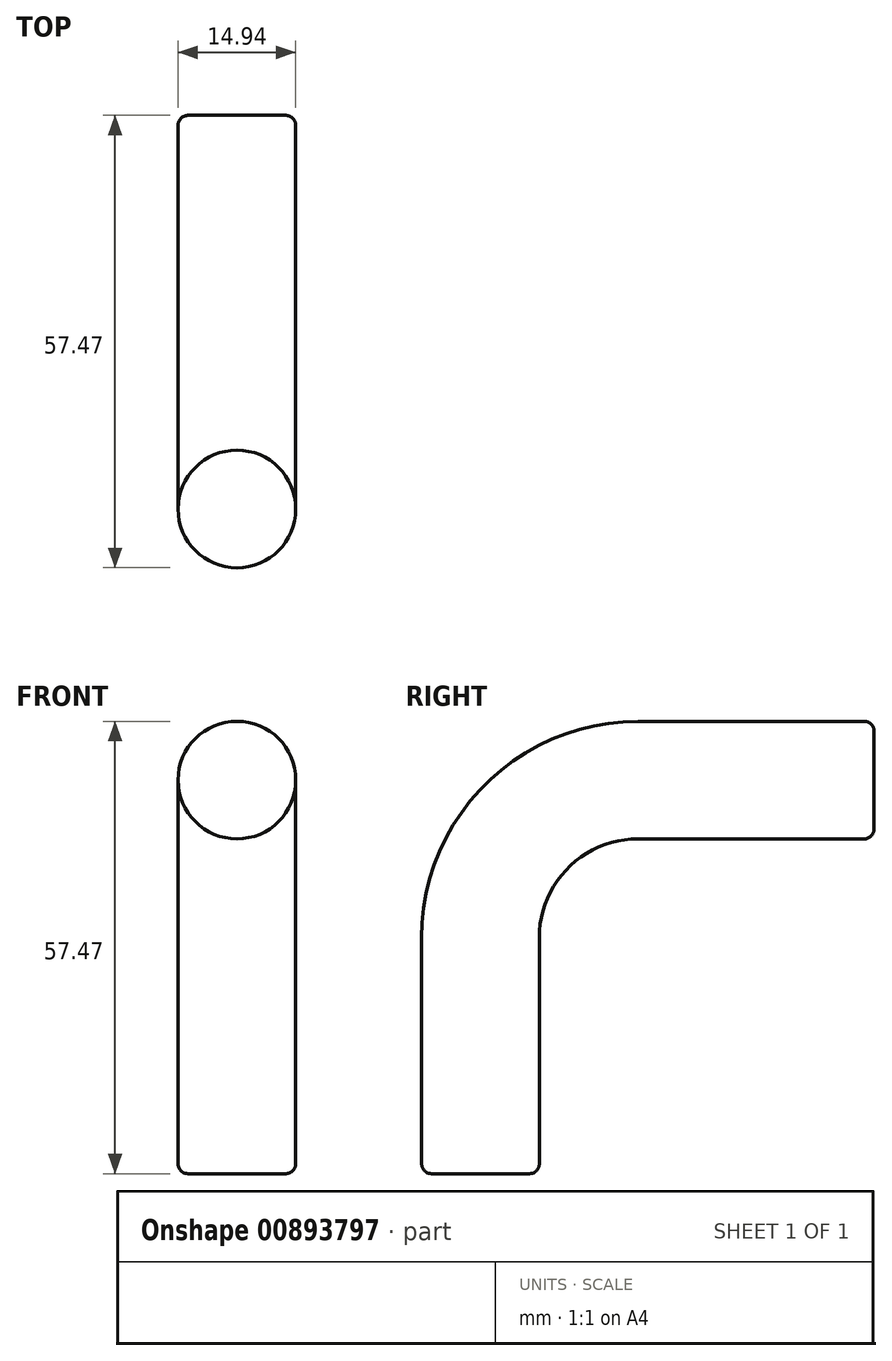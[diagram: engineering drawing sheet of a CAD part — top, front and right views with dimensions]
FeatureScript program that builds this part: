
annotation { "Feature Type Name" : "Feature", "Feature Type Description" : "" }
export const myFeature = defineFeature(function(context is Context, id is Id, definition is map)
    precondition{}
    {
        {
            var Q0;
            Q0=qCreatedBy(makeId("Right.planeOp"),FACE);
            var sketch = newSketch(context, id + "F0", { "sketchPlane" : qUnion([Q0])});
            skLineSegment(sketch, "E0", {"start": v(0, 0) * mm, "end": v(0, 30) * mm});
            skLineSegment(sketch, "E1", {"start": v(20, 50) * mm, "end": v(50, 50) * mm});
            skPoint(sketch, "E2.visualSharp", {"position": v(0, 50) * mm});
            skArc(sketch, "E2.filletArc", {"start": v(20, 50) * mm, "mid": v(5.86, 44.14) * mm, "end": v(0, 30) * mm});
            skSolve(sketch);
        }
        {
            var Q0;
            Q0=qCreatedBy(makeId("Top.planeOp"),FACE);
            var sketch = newSketch(context, id + "F1", { "sketchPlane" : qUnion([Q0])});
            skCircle(sketch, "E3", {"center": v(0, 0) * mm, "radius": 7.47 * mm});
            skSolve(sketch);
        }
        {
            var Q0;
            Q0=makeQuery(id+"F1.imprint","IMPRINT",FACE,{"disambiguationData":[TD([[makeQuery(id+"F1.imprint","IMPRINT",EDGE,{"derivedFrom":sQuery(id+"F1.wireOp",EDGE,"E3")}),1.0]])]});
            var Q1;
            Q1=sQuery(id+"F0.wireOp",EDGE,"E0");
            var Q2;
            Q2=sQuery(id+"F0.wireOp",EDGE,"E2.filletArc");
            var Q3;
            Q3=sQuery(id+"F0.wireOp",EDGE,"E1");
            sweep(context, id + "F2", {"profiles" : qUnion([Q0]), "path" : qUnion([Q1, Q2, Q3])});
        }
        {
            var Q0;
            Q0=makeQuery(id+"F2.opSweep","CAP_EDGE",EDGE,{"disambiguationData":[OSD([sQuery(id+"F0.wireOp",VERTEX,"E1.end"),sQuery(id+"F1.wireOp",EDGE,"E3")])],"isStart":false});
            var Q1;
            Q1=makeQuery(id+"F2.opSweep","CAP_EDGE",EDGE,{"disambiguationData":[OSD([sQuery(id+"F0.wireOp",VERTEX,"E0.start"),sQuery(id+"F1.wireOp",EDGE,"E3")])],"isStart":true});
            fillet(context, id + "F3", {"entities" : qUnion([Q0, Q1]), "radius" : 1.27 * mm, "tangentPropagation" : true, "allowEdgeOverflow" : false});
        }
    });
